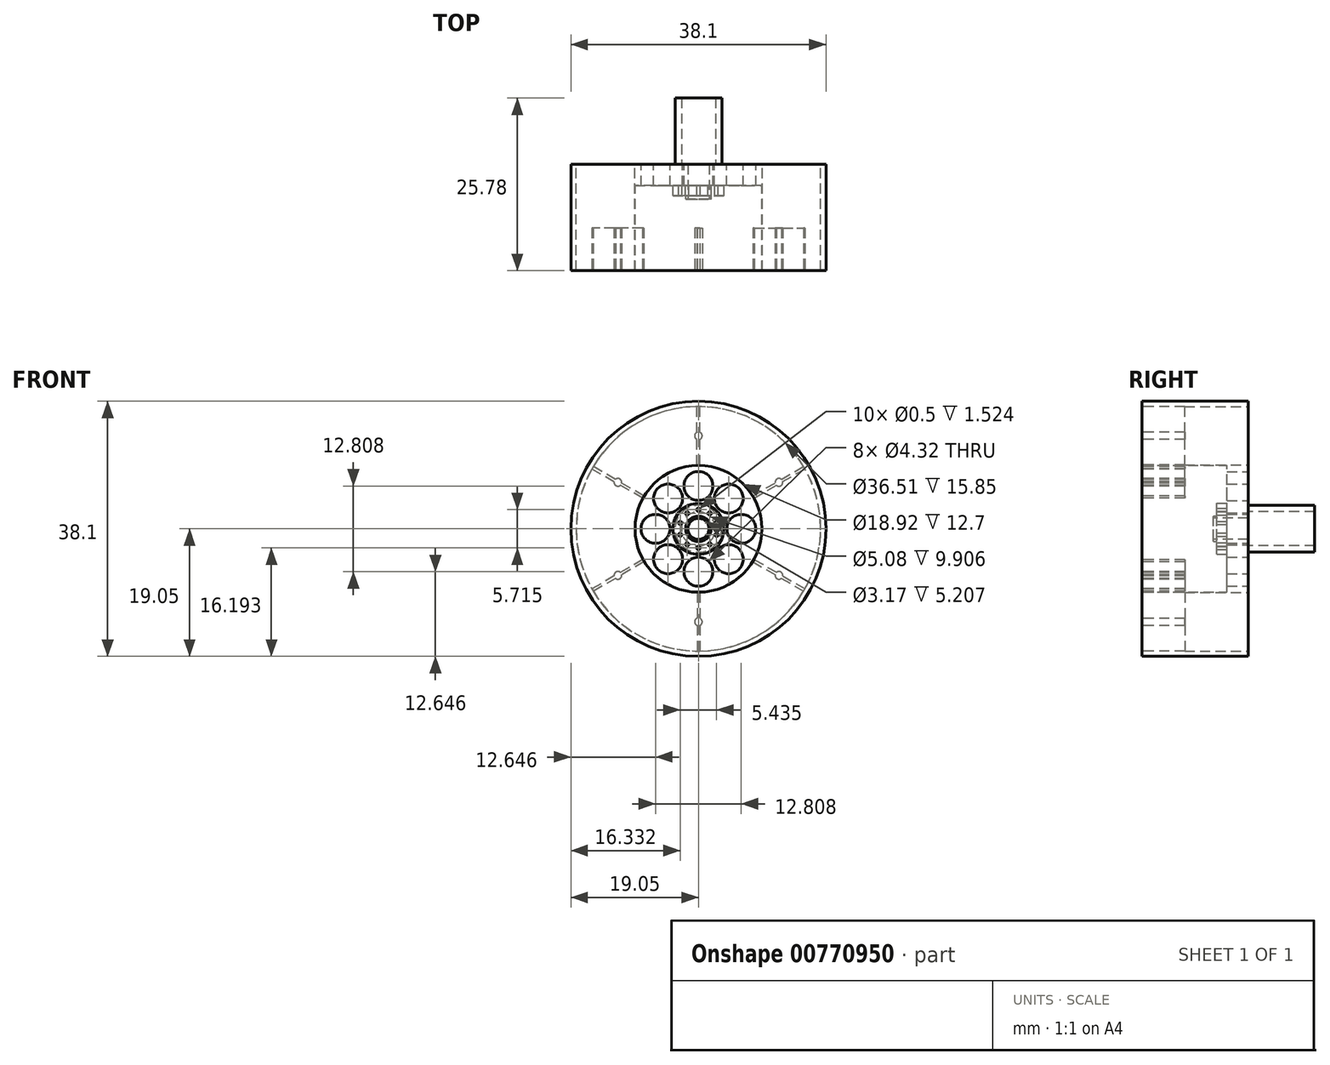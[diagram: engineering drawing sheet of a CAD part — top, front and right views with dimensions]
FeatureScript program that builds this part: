
annotation { "Feature Type Name" : "Feature", "Feature Type Description" : "" }
export const myFeature = defineFeature(function(context is Context, id is Id, definition is map)
    precondition{}
    {
        {
            var Q0;
            Q0=qCreatedBy(makeId("Front.planeOp"),FACE);
            var sketch = newSketch(context, id + "F0", { "sketchPlane" : qUnion([Q0])});
            skCircle(sketch, "E0", {"center": v(0, 0) * mm, "radius": 19.05 * mm});
            skCircle(sketch, "E1", {"center": v(0, 0) * mm, "radius": 17.46 * mm});
            skSolve(sketch);
        }
        {
            var Q0;
            Q0=qSketchRegion(id+"F0",true);
            extrude(context, id + "F1", {"entities" : qUnion([Q0]), "oppositeDirection" : true, "depth" : 15.88 * mm, "offsetDistance" : 25.4 * mm});
        }
        {
            var Q0;
            Q0=makeQuery(id+"F0.imprint","IMPRINT",FACE,{"disambiguationData":[TD([[makeQuery(id+"F0.imprint","IMPRINT",EDGE,{"derivedFrom":sQuery(id+"F0.wireOp",EDGE,"E1")}),1.0]])]});
            extrude(context, id + "F2", {"entities" : qUnion([Q0]), "operationType" : NewBodyOperationType.ADD, "oppositeDirection" : true, "depth" : 15.88 * mm, "offsetDistance" : 25.4 * mm});
        }
        {
            var Q0;
            {var subQ0=sQuery(id+"F0.wireOp",EDGE,"E1");Q0=makeQuery(id+"F2.boolean.opBoolean","MERGE",FACE,{"derivedFrom":[makeQuery(id+"F1.opExtrude","CAP_FACE",FACE,{"disambiguationData":[OSD([sQuery(id+"F0.wireOp",EDGE,"E0"),subQ0])],"isStart":true}),makeQuery(id+"F2.opExtrude","CAP_FACE",FACE,{"disambiguationData":[OSD([subQ0])],"isStart":true})]});}
            var sketch = newSketch(context, id + "F3", { "sketchPlane" : qUnion([Q0])});
            skCircle(sketch, "E2", {"center": v(0, 0) * mm, "radius": 9.53 * mm});
            skSolve(sketch);
        }
        {
            var Q0;
            Q0=makeQuery(id+"F3.imprint","IMPRINT",FACE,{"disambiguationData":[TD([[makeQuery(id+"F3.imprint","IMPRINT",EDGE,{"derivedFrom":sQuery(id+"F3.wireOp",EDGE,"E2")}),1.0]])]});
            extrude(context, id + "F4", {"entities" : qUnion([Q0]), "operationType" : NewBodyOperationType.REMOVE, "oppositeDirection" : true, "depth" : 12.7 * mm, "offsetDistance" : 25.4 * mm});
        }
        {
            var Q0;
            {var subQ0=sQuery(id+"F0.wireOp",EDGE,"E1");Q0=makeQuery(id+"F2.boolean.opBoolean","MERGE",FACE,{"derivedFrom":[makeQuery(id+"F1.opExtrude","CAP_FACE",FACE,{"disambiguationData":[OSD([sQuery(id+"F0.wireOp",EDGE,"E0"),subQ0])],"isStart":false}),makeQuery(id+"F2.opExtrude","CAP_FACE",FACE,{"disambiguationData":[OSD([subQ0])],"isStart":false})]});}
            var sketch = newSketch(context, id + "F5", { "sketchPlane" : qUnion([Q0])});
            skCircle(sketch, "E3", {"center": v(0, 0) * mm, "radius": 18.26 * mm});
            skCircle(sketch, "E4", {"center": v(0, 0) * mm, "radius": 9.53 * mm});
            skSolve(sketch);
        }
        {
            var Q0;
            Q0=makeQuery(id+"F5.imprint","IMPRINT",FACE,{"disambiguationData":[TD([[makeQuery(id+"F5.imprint","IMPRINT",EDGE,{"derivedFrom":sQuery(id+"F5.wireOp",EDGE,"E3")}),1.0]])]});
            extrude(context, id + "F6", {"entities" : qUnion([Q0]), "operationType" : NewBodyOperationType.REMOVE, "oppositeDirection" : true, "depth" : 15.85 * mm, "offsetDistance" : 25.4 * mm});
        }
        {
            var Q0;
            Q0=makeQuery(id+"F4.boolean.opBoolean","COPY",FACE,{"derivedFrom":makeQuery(id+"F4.opExtrude","CAP_FACE",FACE,{"disambiguationData":[OSD([sQuery(id+"F3.wireOp",EDGE,"E2")])],"isStart":false})});
            var sketch = newSketch(context, id + "F7", { "sketchPlane" : qUnion([Q0])});
            skCircle(sketch, "E5", {"center": v(0, 0) * mm, "radius": 9.52 * mm});
            skCircle(sketch, "E6", {"center": v(0, 0) * mm, "radius": 9.46 * mm});
            skSolve(sketch);
        }
        {
            var Q0;
            Q0=makeQuery(id+"F7.imprint","IMPRINT",FACE,{"disambiguationData":[TD([[makeQuery(id+"F7.imprint","IMPRINT",EDGE,{"derivedFrom":sQuery(id+"F7.wireOp",EDGE,"E5")}),1.0]])]});
            var Q1;
            Q1=sQuery(id+"F7.wireOp",EDGE,"E5");
            extrude(context, id + "F8", {"entities" : qUnion([Q0]), "operationType" : NewBodyOperationType.ADD, "surfaceEntities" : qUnion([Q1]), "depth" : 12.7 * mm, "offsetDistance" : 25.4 * mm, "surfaceOperationType" : NewSurfaceOperationType.ADD});
        }
        {
            var Q0;
            {var subQ0=sQuery(id+"F0.wireOp",EDGE,"E1");Q0=makeQuery(id+"F6.boolean.opBoolean","SPLIT",FACE,{"disambiguationData":[TD([makeQuery(id+"F6.opExtrude","SWEPT_FACE",FACE,{"disambiguationData":[OSD([sQuery(id+"F5.wireOp",EDGE,"E4")])]})])],"derivedFrom":makeQuery(id+"F2.boolean.opBoolean","MERGE",FACE,{"derivedFrom":[makeQuery(id+"F1.opExtrude","CAP_FACE",FACE,{"disambiguationData":[OSD([sQuery(id+"F0.wireOp",EDGE,"E0"),subQ0])],"isStart":false}),makeQuery(id+"F2.opExtrude","CAP_FACE",FACE,{"disambiguationData":[OSD([subQ0])],"isStart":false})]})});}
            var sketch = newSketch(context, id + "F9", { "sketchPlane" : qUnion([Q0])});
            skLineSegment(sketch, "E7", {"start": v(0, 6) * mm, "end": v(0, 6.2) * mm});
            skLineSegment(sketch, "E8", {"start": v(0, 6.2) * mm, "end": v(0, 6.4) * mm});
            skCircle(sketch, "E9", {"center": v(0, 6.4) * mm, "radius": 2.16 * mm});
            skCircle(sketch, "E10.1.0", {"center": v(-4.53, 4.53) * mm, "radius": 2.16 * mm});
            skCircle(sketch, "E10.2.0", {"center": v(-6.4, 0) * mm, "radius": 2.16 * mm});
            skCircle(sketch, "E10.3.0", {"center": v(-4.53, -4.53) * mm, "radius": 2.16 * mm});
            skCircle(sketch, "E10.4.0", {"center": v(0, -6.4) * mm, "radius": 2.16 * mm});
            skCircle(sketch, "E10.5.0", {"center": v(4.53, -4.53) * mm, "radius": 2.16 * mm});
            skCircle(sketch, "E10.6.0", {"center": v(6.4, 0) * mm, "radius": 2.16 * mm});
            skCircle(sketch, "E10.7.0", {"center": v(4.53, 4.53) * mm, "radius": 2.16 * mm});
            skPoint(sketch, "E10.center", {"position": v(0, 0) * mm});
            skSolve(sketch);
        }
        {
            var Q0;
            Q0=makeQuery(id+"F9.imprint","IMPRINT",FACE,{"disambiguationData":[TD([[makeQuery(id+"F9.imprint","IMPRINT",EDGE,{"derivedFrom":sQuery(id+"F9.wireOp",EDGE,"E10.1.0")}),1.0]])]});
            var Q1;
            Q1=makeQuery(id+"F9.imprint","IMPRINT",FACE,{"disambiguationData":[TD([[makeQuery(id+"F9.imprint","IMPRINT",EDGE,{"derivedFrom":sQuery(id+"F9.wireOp",EDGE,"E10.2.0")}),1.0]])]});
            var Q2;
            Q2=makeQuery(id+"F9.imprint","IMPRINT",FACE,{"disambiguationData":[TD([[makeQuery(id+"F9.imprint","IMPRINT",EDGE,{"derivedFrom":sQuery(id+"F9.wireOp",EDGE,"E10.3.0")}),1.0]])]});
            var Q3;
            Q3=makeQuery(id+"F9.imprint","IMPRINT",FACE,{"disambiguationData":[TD([[makeQuery(id+"F9.imprint","IMPRINT",EDGE,{"derivedFrom":sQuery(id+"F9.wireOp",EDGE,"E10.4.0")}),1.0]])]});
            var Q4;
            Q4=makeQuery(id+"F9.imprint","IMPRINT",FACE,{"disambiguationData":[TD([[makeQuery(id+"F9.imprint","IMPRINT",EDGE,{"derivedFrom":sQuery(id+"F9.wireOp",EDGE,"E10.5.0")}),1.0]])]});
            var Q5;
            Q5=makeQuery(id+"F9.imprint","IMPRINT",FACE,{"disambiguationData":[TD([[makeQuery(id+"F9.imprint","IMPRINT",EDGE,{"derivedFrom":sQuery(id+"F9.wireOp",EDGE,"E10.6.0")}),1.0]])]});
            var Q6;
            Q6=makeQuery(id+"F9.imprint","IMPRINT",FACE,{"disambiguationData":[TD([[makeQuery(id+"F9.imprint","IMPRINT",EDGE,{"derivedFrom":sQuery(id+"F9.wireOp",EDGE,"E10.7.0")}),1.0]])]});
            var Q7;
            Q7=makeQuery(id+"F9.imprint","IMPRINT",FACE,{"disambiguationData":[TD([[makeQuery(id+"F9.imprint","IMPRINT",EDGE,{"derivedFrom":sQuery(id+"F9.wireOp",EDGE,"E9")}),1.0]])]});
            extrude(context, id + "F10", {"entities" : qUnion([Q0, Q1, Q2, Q3, Q4, Q5, Q6, Q7]), "operationType" : NewBodyOperationType.REMOVE, "oppositeDirection" : true, "depth" : 25.4 * mm, "offsetDistance" : 25.4 * mm});
        }
        {
            var Q0;
            Q0=makeQuery(id+"F4.boolean.opBoolean","COPY",FACE,{"derivedFrom":makeQuery(id+"F4.opExtrude","CAP_FACE",FACE,{"disambiguationData":[OSD([sQuery(id+"F3.wireOp",EDGE,"E2")])],"isStart":false})});
            var sketch = newSketch(context, id + "F11", { "sketchPlane" : qUnion([Q0])});
            skCircle(sketch, "E11", {"center": v(0, 0) * mm, "radius": 3.8 * mm});
            skCircle(sketch, "E12", {"center": v(0, 0) * mm, "radius": 1.9 * mm});
            skLineSegment(sketch, "E13", {"start": v(0, 1.9) * mm, "end": v(0, 2.86) * mm});
            skCircle(sketch, "E14", {"center": v(0, 2.86) * mm, "radius": 0.25 * mm});
            skCircle(sketch, "E15.1.0", {"center": v(-1.68, 2.31) * mm, "radius": 0.25 * mm});
            skCircle(sketch, "E15.2.0", {"center": v(-2.72, 0.88) * mm, "radius": 0.25 * mm});
            skCircle(sketch, "E15.3.0", {"center": v(-2.72, -0.88) * mm, "radius": 0.25 * mm});
            skCircle(sketch, "E15.4.0", {"center": v(-1.68, -2.31) * mm, "radius": 0.25 * mm});
            skCircle(sketch, "E15.5.0", {"center": v(0, -2.86) * mm, "radius": 0.25 * mm});
            skCircle(sketch, "E15.6.0", {"center": v(1.68, -2.31) * mm, "radius": 0.25 * mm});
            skCircle(sketch, "E15.7.0", {"center": v(2.72, -0.88) * mm, "radius": 0.25 * mm});
            skCircle(sketch, "E15.8.0", {"center": v(2.72, 0.88) * mm, "radius": 0.25 * mm});
            skCircle(sketch, "E15.9.0", {"center": v(1.68, 2.31) * mm, "radius": 0.25 * mm});
            skSolve(sketch);
        }
        {
            var Q0;
            Q0=makeQuery(id+"F11.imprint","IMPRINT",FACE,{"disambiguationData":[TD([[makeQuery(id+"F11.imprint","IMPRINT",EDGE,{"derivedFrom":sQuery(id+"F11.wireOp",EDGE,"E11")}),1.0]])]});
            extrude(context, id + "F12", {"entities" : qUnion([Q0]), "operationType" : NewBodyOperationType.ADD, "depth" : 1.52 * mm, "offsetDistance" : 25.4 * mm});
        }
        {
            var Q0;
            Q0=makeQuery(id+"F12.boolean.opBoolean","SPLIT",FACE,{"disambiguationData":[TD([makeQuery(id+"F12.opExtrude","SWEPT_FACE",FACE,{"disambiguationData":[OSD([sQuery(id+"F11.wireOp",EDGE,"E12")])]})])],"derivedFrom":makeQuery(id+"F4.boolean.opBoolean","COPY",FACE,{"derivedFrom":makeQuery(id+"F4.opExtrude","CAP_FACE",FACE,{"disambiguationData":[OSD([sQuery(id+"F3.wireOp",EDGE,"E2")])],"isStart":false})})});
            extrude(context, id + "F13", {"entities" : qUnion([Q0]), "operationType" : NewBodyOperationType.ADD, "depth" : 2.03 * mm, "offsetDistance" : 25.4 * mm});
        }
        {
            var Q0;
            {var subQ0=sQuery(id+"F0.wireOp",EDGE,"E1");Q0=makeQuery(id+"F6.boolean.opBoolean","SPLIT",FACE,{"disambiguationData":[TD([makeQuery(id+"F6.opExtrude","SWEPT_FACE",FACE,{"disambiguationData":[OSD([sQuery(id+"F5.wireOp",EDGE,"E4")])]})])],"derivedFrom":makeQuery(id+"F2.boolean.opBoolean","MERGE",FACE,{"derivedFrom":[makeQuery(id+"F1.opExtrude","CAP_FACE",FACE,{"disambiguationData":[OSD([sQuery(id+"F0.wireOp",EDGE,"E0"),subQ0])],"isStart":false}),makeQuery(id+"F2.opExtrude","CAP_FACE",FACE,{"disambiguationData":[OSD([subQ0])],"isStart":false})]})});}
            var sketch = newSketch(context, id + "F14", { "sketchPlane" : qUnion([Q0])});
            skCircle(sketch, "E16", {"center": v(0, 0) * mm, "radius": 3.5 * mm});
            skCircle(sketch, "E17", {"center": v(0, 0) * mm, "radius": 2.54 * mm});
            skSolve(sketch);
        }
        {
            var Q0;
            Q0=makeQuery(id+"F14.imprint","IMPRINT",FACE,{"disambiguationData":[TD([[makeQuery(id+"F14.imprint","IMPRINT",EDGE,{"derivedFrom":sQuery(id+"F14.wireOp",EDGE,"E16")}),1.0]])]});
            extrude(context, id + "F15", {"entities" : qUnion([Q0]), "operationType" : NewBodyOperationType.ADD, "depth" : 9.9 * mm, "offsetDistance" : 25.4 * mm});
        }
        {
            var Q0;
            Q0=makeQuery(id+"F6.boolean.opBoolean","COPY",FACE,{"derivedFrom":makeQuery(id+"F6.opExtrude","CAP_FACE",FACE,{"disambiguationData":[OSD([sQuery(id+"F5.wireOp",EDGE,"E3"),sQuery(id+"F5.wireOp",EDGE,"E4")])],"isStart":false})});
            var sketch = newSketch(context, id + "F16", { "sketchPlane" : qUnion([Q0])});
            skLineSegment(sketch, "E18", {"start": v(0, 9.53) * mm, "end": v(0.21, 9.52) * mm});
            skLineSegment(sketch, "E19", {"start": v(0, 9.53) * mm, "end": v(-0.2, 9.52) * mm});
            skLineSegment(sketch, "E20", {"start": v(-0.2, 9.52) * mm, "end": v(-0.2, 13.35) * mm});
            skLineSegment(sketch, "E21", {"start": v(0.21, 9.52) * mm, "end": v(0.21, 13.36) * mm});
            skPoint(sketch, "E22.endSnap0", {"position": v(0.21, 13.89) * mm});
            skArc(sketch, "E23", {"start": v(-0.2, 14.43) * mm, "mid": v(-0.57, 13.89) * mm, "end": v(-0.2, 13.35) * mm});
            skArc(sketch, "E24.trimOffspring", {"start": v(0.21, 13.36) * mm, "mid": v(0.57, 13.89) * mm, "end": v(0.21, 14.42) * mm});
            skLineSegment(sketch, "E25.trimOffspring", {"start": v(-0.2, 14.43) * mm, "end": v(-0.2, 18.26) * mm});
            skLineSegment(sketch, "E26.trimOffspring", {"start": v(0.21, 14.42) * mm, "end": v(0.21, 18.26) * mm});
            skLineSegment(sketch, "E27.1.0", {"start": v(-12.6, 7.05) * mm, "end": v(-15.9, 8.96) * mm});
            skLineSegment(sketch, "E27.1.1", {"start": v(-12.38, 7.4) * mm, "end": v(-15.7, 9.3) * mm});
            skArc(sketch, "E27.1.2", {"start": v(-12.6, 7.05) * mm, "mid": v(-12.31, 6.45) * mm, "end": v(-11.66, 6.5) * mm});
            skArc(sketch, "E27.1.3", {"start": v(-11.46, 6.86) * mm, "mid": v(-11.74, 7.44) * mm, "end": v(-12.38, 7.4) * mm});
            skLineSegment(sketch, "E27.1.4", {"start": v(-8.14, 4.94) * mm, "end": v(-11.46, 6.86) * mm});
            skLineSegment(sketch, "E27.1.5", {"start": v(-8.34, 4.6) * mm, "end": v(-11.66, 6.5) * mm});
            skLineSegment(sketch, "E27.2.0", {"start": v(-12.4, -7.38) * mm, "end": v(-15.71, -9.3) * mm});
            skLineSegment(sketch, "E27.2.1", {"start": v(-12.6, -7.03) * mm, "end": v(-15.91, -8.95) * mm});
            skArc(sketch, "E27.2.2", {"start": v(-12.4, -7.38) * mm, "mid": v(-11.74, -7.44) * mm, "end": v(-11.47, -6.84) * mm});
            skArc(sketch, "E27.2.3", {"start": v(-11.67, -6.5) * mm, "mid": v(-12.31, -6.45) * mm, "end": v(-12.6, -7.03) * mm});
            skLineSegment(sketch, "E27.2.4", {"start": v(-8.35, -4.58) * mm, "end": v(-11.67, -6.5) * mm});
            skLineSegment(sketch, "E27.2.5", {"start": v(-8.15, -4.93) * mm, "end": v(-11.47, -6.84) * mm});
            skLineSegment(sketch, "E27.3.0", {"start": v(0.2, -14.43) * mm, "end": v(0.2, -18.26) * mm});
            skLineSegment(sketch, "E27.3.1", {"start": v(-0.21, -14.42) * mm, "end": v(-0.21, -18.26) * mm});
            skArc(sketch, "E27.3.2", {"start": v(0.2, -14.43) * mm, "mid": v(0.57, -13.89) * mm, "end": v(0.2, -13.35) * mm});
            skArc(sketch, "E27.3.3", {"start": v(-0.21, -13.36) * mm, "mid": v(-0.57, -13.89) * mm, "end": v(-0.21, -14.42) * mm});
            skLineSegment(sketch, "E27.3.4", {"start": v(-0.21, -9.52) * mm, "end": v(-0.21, -13.36) * mm});
            skLineSegment(sketch, "E27.3.5", {"start": v(0.2, -9.52) * mm, "end": v(0.2, -13.35) * mm});
            skLineSegment(sketch, "E27.4.0", {"start": v(12.6, -7.05) * mm, "end": v(15.9, -8.96) * mm});
            skLineSegment(sketch, "E27.4.1", {"start": v(12.38, -7.4) * mm, "end": v(15.7, -9.3) * mm});
            skArc(sketch, "E27.4.2", {"start": v(12.6, -7.05) * mm, "mid": v(12.31, -6.45) * mm, "end": v(11.66, -6.5) * mm});
            skArc(sketch, "E27.4.3", {"start": v(11.46, -6.86) * mm, "mid": v(11.74, -7.44) * mm, "end": v(12.38, -7.4) * mm});
            skLineSegment(sketch, "E27.4.4", {"start": v(8.14, -4.94) * mm, "end": v(11.46, -6.86) * mm});
            skLineSegment(sketch, "E27.4.5", {"start": v(8.34, -4.6) * mm, "end": v(11.66, -6.5) * mm});
            skLineSegment(sketch, "E27.5.0", {"start": v(12.4, 7.38) * mm, "end": v(15.71, 9.3) * mm});
            skLineSegment(sketch, "E27.5.1", {"start": v(12.6, 7.03) * mm, "end": v(15.91, 8.95) * mm});
            skArc(sketch, "E27.5.2", {"start": v(12.4, 7.38) * mm, "mid": v(11.74, 7.44) * mm, "end": v(11.47, 6.84) * mm});
            skArc(sketch, "E27.5.3", {"start": v(11.67, 6.5) * mm, "mid": v(12.31, 6.45) * mm, "end": v(12.6, 7.03) * mm});
            skLineSegment(sketch, "E27.5.4", {"start": v(8.35, 4.58) * mm, "end": v(11.67, 6.5) * mm});
            skLineSegment(sketch, "E27.5.5", {"start": v(8.15, 4.93) * mm, "end": v(11.47, 6.84) * mm});
            skPoint(sketch, "E27.center", {"position": v(0, 0) * mm});
            skSolve(sketch);
        }
        {
            var Q0;
            {var subQ4=sQuery(id+"F16.wireOp",EDGE,"E20");Q0=makeQuery(id+"F16.imprint","IMPRINT",FACE,{"disambiguationData":[TD([[makeQuery(id+"F16.imprint","IMPRINT",EDGE,{"derivedFrom":subQ4}),-1.0]])]});}
            var Q1;
            {var subQ4=sQuery(id+"F16.wireOp",EDGE,"E27.1.0");Q1=makeQuery(id+"F16.imprint","IMPRINT",FACE,{"disambiguationData":[TD([[makeQuery(id+"F16.imprint","IMPRINT",EDGE,{"derivedFrom":subQ4}),-1.0]])]});}
            var Q2;
            {var subQ1=sQuery(id+"F16.wireOp",EDGE,"E27.2.0");Q2=makeQuery(id+"F16.imprint","IMPRINT",FACE,{"disambiguationData":[TD([[makeQuery(id+"F16.imprint","IMPRINT",EDGE,{"derivedFrom":subQ1}),-1.0]])]});}
            var Q3;
            {var subQ0=sQuery(id+"F16.wireOp",EDGE,"E27.3.0");Q3=makeQuery(id+"F16.imprint","IMPRINT",FACE,{"disambiguationData":[TD([[makeQuery(id+"F16.imprint","IMPRINT",EDGE,{"derivedFrom":subQ0}),-1.0]])]});}
            var Q4;
            {var subQ4=sQuery(id+"F16.wireOp",EDGE,"E27.4.0");Q4=makeQuery(id+"F16.imprint","IMPRINT",FACE,{"disambiguationData":[TD([[makeQuery(id+"F16.imprint","IMPRINT",EDGE,{"derivedFrom":subQ4}),-1.0]])]});}
            var Q5;
            {var subQ1=sQuery(id+"F16.wireOp",EDGE,"E27.5.0");Q5=makeQuery(id+"F16.imprint","IMPRINT",FACE,{"disambiguationData":[TD([[makeQuery(id+"F16.imprint","IMPRINT",EDGE,{"derivedFrom":subQ1}),-1.0]])]});}
            extrude(context, id + "F17", {"entities" : qUnion([Q0, Q1, Q2, Q3, Q4, Q5]), "operationType" : NewBodyOperationType.ADD, "depth" : 6.35 * mm, "offsetDistance" : 25.4 * mm});
        }
        {
            var Q0;
            Q0=makeQuery(id+"F13.opExtrude","CAP_FACE",FACE,{"disambiguationData":[OSD([sQuery(id+"F3.wireOp",EDGE,"E2")])],"isStart":false});
            var sketch = newSketch(context, id + "F18", { "sketchPlane" : qUnion([Q0])});
            skCircle(sketch, "E28", {"center": v(0, 0) * mm, "radius": 1.59 * mm});
            skSolve(sketch);
        }
        {
            var Q0;
            Q0=makeQuery(id+"F18.imprint","IMPRINT",FACE,{"disambiguationData":[TD([[makeQuery(id+"F18.imprint","IMPRINT",EDGE,{"derivedFrom":sQuery(id+"F18.wireOp",EDGE,"E28")}),1.0]])]});
            extrude(context, id + "F19", {"entities" : qUnion([Q0]), "operationType" : NewBodyOperationType.REMOVE, "oppositeDirection" : true, "depth" : 25.4 * mm, "offsetDistance" : 25.4 * mm});
        }
    });
